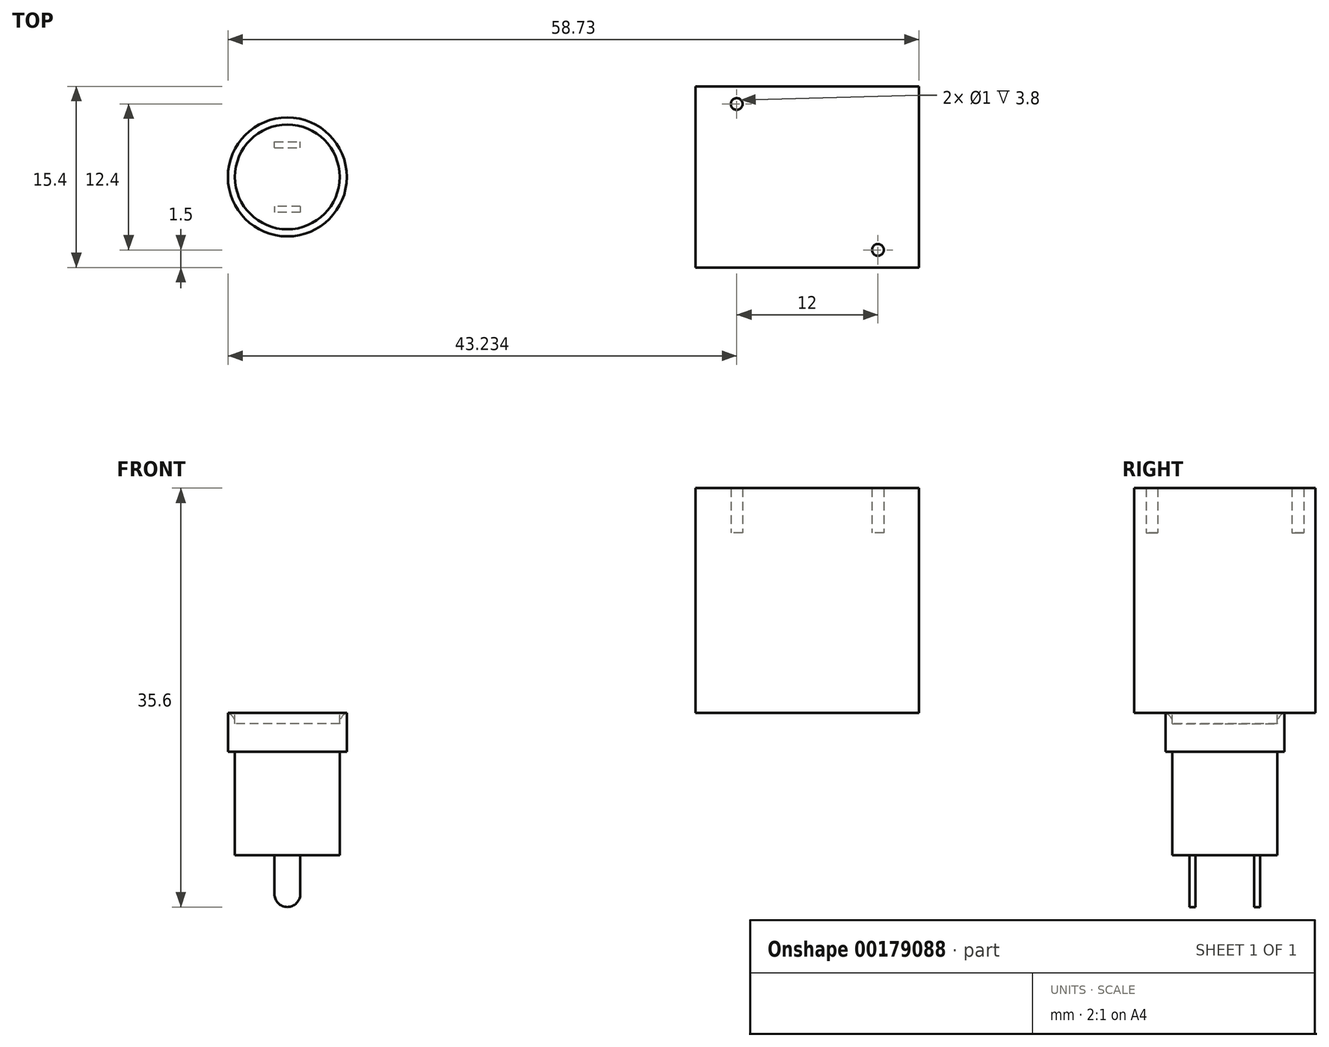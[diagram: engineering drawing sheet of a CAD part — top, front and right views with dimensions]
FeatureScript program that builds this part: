
annotation { "Feature Type Name" : "Feature", "Feature Type Description" : "" }
export const myFeature = defineFeature(function(context is Context, id is Id, definition is map)
    precondition{}
    {
        {
            var Q0;
            Q0=qCreatedBy(makeId("Top.planeOp"),FACE);
            var sketch = newSketch(context, id + "F0", { "sketchPlane" : qUnion([Q0])});
            skCircle(sketch, "E0", {"center": v(0, 0) * mm, "radius": 4.45 * mm});
            skCircle(sketch, "E1", {"center": v(0, 0) * mm, "radius": 5.05 * mm});
            skSolve(sketch);
        }
        {
            var Q0;
            Q0=makeQuery(id+"F0.imprint","IMPRINT",FACE,{"disambiguationData":[TD([[makeQuery(id+"F0.imprint","IMPRINT",EDGE,{"derivedFrom":sQuery(id+"F0.wireOp",EDGE,"E0")}),-1.0]])]});
            extrude(context, id + "F1", {"entities" : qUnion([Q0]), "oppositeDirection" : true, "depth" : 3.3 * mm});
        }
        {
            var Q0;
            Q0=makeQuery(id+"F1.opExtrude","CAP_EDGE",EDGE,{"disambiguationData":[OSD([sQuery(id+"F0.wireOp",EDGE,"E0")])],"isStart":true});
            fillet(context, id + "F2", {"entities" : qUnion([Q0]), "radius" : 1 * mm, "tangentPropagation" : true, "allowEdgeOverflow" : false});
        }
        {
            var Q0;
            Q0=makeQuery(id+"F0.imprint","IMPRINT",FACE,{"disambiguationData":[TD([[makeQuery(id+"F0.imprint","IMPRINT",EDGE,{"derivedFrom":sQuery(id+"F0.wireOp",EDGE,"E0")}),1.0]])]});
            extrude(context, id + "F3", {"entities" : qUnion([Q0]), "operationType" : NewBodyOperationType.ADD, "oppositeDirection" : true, "depth" : 12.1 * mm});
        }
        {
            var Q0;
            Q0=makeQuery(id+"F3.opExtrude","CAP_FACE",FACE,{"disambiguationData":[OSD([sQuery(id+"F0.wireOp",EDGE,"E0")])],"isStart":false});
            var sketch = newSketch(context, id + "F4", { "sketchPlane" : qUnion([Q0])});
            skLineSegment(sketch, "E2", {"start": v(0, 0) * mm, "end": v(0, 2.5) * mm, "construction": true});
            skLineSegment(sketch, "E3", {"start": v(0, 2.5) * mm, "end": v(1.1, 2.5) * mm});
            skLineSegment(sketch, "E4", {"start": v(1.1, 2.5) * mm, "end": v(1.1, 3) * mm});
            skLineSegment(sketch, "E5", {"start": v(1.1, 3) * mm, "end": v(0, 3) * mm});
            skPoint(sketch, "E5.endSnap0", {"position": v(0, 1.25) * mm});
            skLineSegment(sketch, "E6.MirrorCS", {"start": v(-1.1, 3) * mm, "end": v(0, 3) * mm});
            skLineSegment(sketch, "E7.MirrorCS", {"start": v(0, 2.5) * mm, "end": v(-1.1, 2.5) * mm});
            skLineSegment(sketch, "E8.MirrorCS", {"start": v(-1.1, 2.5) * mm, "end": v(-1.1, 3) * mm});
            skLineSegment(sketch, "E9", {"start": v(0, 0) * mm, "end": v(4.45, 0) * mm, "construction": true});
            skLineSegment(sketch, "E10.MirrorCS", {"start": v(-1.1, -3) * mm, "end": v(0, -3) * mm});
            skLineSegment(sketch, "E11.MirrorCS", {"start": v(1.1, -3) * mm, "end": v(0, -3) * mm});
            skLineSegment(sketch, "E12.MirrorCS", {"start": v(1.1, -2.5) * mm, "end": v(1.1, -3) * mm});
            skLineSegment(sketch, "E13.MirrorCS", {"start": v(0, -2.5) * mm, "end": v(1.1, -2.5) * mm});
            skLineSegment(sketch, "E14.MirrorCS", {"start": v(0, -2.5) * mm, "end": v(-1.1, -2.5) * mm});
            skLineSegment(sketch, "E15.MirrorCS", {"start": v(-1.1, -2.5) * mm, "end": v(-1.1, -3) * mm});
            skSolve(sketch);
        }
        {
            var Q0;
            Q0=makeQuery(id+"F4.imprint","IMPRINT",FACE,{"disambiguationData":[TD([[makeQuery(id+"F4.imprint","IMPRINT",EDGE,{"derivedFrom":sQuery(id+"F4.wireOp",EDGE,"E4")}),1.0]])]});
            var Q1;
            Q1=makeQuery(id+"F4.imprint","IMPRINT",FACE,{"disambiguationData":[TD([[makeQuery(id+"F4.imprint","IMPRINT",EDGE,{"derivedFrom":sQuery(id+"F4.wireOp",EDGE,"E10.MirrorCS")}),1.0]])]});
            extrude(context, id + "F5", {"entities" : qUnion([Q0, Q1]), "operationType" : NewBodyOperationType.ADD, "depth" : 4.4 * mm});
        }
        {
            var Q0;
            Q0=makeQuery(id+"F5.opExtrude","CAP_EDGE",EDGE,{"disambiguationData":[OSD([sQuery(id+"F4.wireOp",EDGE,"E8.MirrorCS")])],"isStart":false});
            var Q1;
            Q1=makeQuery(id+"F5.opExtrude","CAP_EDGE",EDGE,{"disambiguationData":[OSD([sQuery(id+"F4.wireOp",EDGE,"E4")])],"isStart":false});
            var Q2;
            Q2=makeQuery(id+"F5.opExtrude","CAP_EDGE",EDGE,{"disambiguationData":[OSD([sQuery(id+"F4.wireOp",EDGE,"E12.MirrorCS")])],"isStart":false});
            var Q3;
            Q3=makeQuery(id+"F5.opExtrude","CAP_EDGE",EDGE,{"disambiguationData":[OSD([sQuery(id+"F4.wireOp",EDGE,"E15.MirrorCS")])],"isStart":false});
            fillet(context, id + "F6", {"entities" : qUnion([Q0, Q1, Q2, Q3]), "radius" : 1.1 * mm, "tangentPropagation" : true, "allowEdgeOverflow" : false});
        }
        {
            var Q0;
            Q0=qCreatedBy(makeId("Top.planeOp"),FACE);
            var sketch = newSketch(context, id + "F7", { "sketchPlane" : qUnion([Q0])});
            skLineSegment(sketch, "E16.bottom", {"start": v(53.68, 7.7) * mm, "end": v(34.68, 7.7) * mm});
            skLineSegment(sketch, "E16.top", {"start": v(53.68, -7.7) * mm, "end": v(34.68, -7.7) * mm});
            skLineSegment(sketch, "E16.left", {"start": v(53.68, 7.7) * mm, "end": v(53.68, -7.7) * mm});
            skLineSegment(sketch, "E16.right", {"start": v(34.68, 7.7) * mm, "end": v(34.68, -7.7) * mm});
            skPoint(sketch, "E16.middle", {"position": v(44.18, 0) * mm});
            skSolve(sketch);
        }
        {
            var Q0;
            Q0=makeQuery(id+"F7.imprint","IMPRINT",FACE,{"disambiguationData":[TD([[makeQuery(id+"F7.imprint","IMPRINT",EDGE,{"derivedFrom":sQuery(id+"F7.wireOp",EDGE,"E16.bottom")}),1.0]])]});
            extrude(context, id + "F8", {"entities" : qUnion([Q0]), "depth" : 15.3 * mm});
        }
        {
            var Q0;
            Q0=makeQuery(id+"F8.opExtrude","CAP_FACE",FACE,{"disambiguationData":[OSD([sQuery(id+"F7.wireOp",EDGE,"E16.bottom"),sQuery(id+"F7.wireOp",EDGE,"E16.top"),sQuery(id+"F7.wireOp",EDGE,"E16.left"),sQuery(id+"F7.wireOp",EDGE,"E16.right")])],"isStart":false});
            var sketch = newSketch(context, id + "F9", { "sketchPlane" : qUnion([Q0])});
            skCircle(sketch, "E17", {"center": v(50.18, 6.2) * mm, "radius": 0.5 * mm});
            skLineSegment(sketch, "E18", {"start": v(50.18, 6.2) * mm, "end": v(50.18, 7.7) * mm, "construction": true});
            skLineSegment(sketch, "E19", {"start": v(50.18, 7.7) * mm, "end": v(53.68, 7.7) * mm, "construction": true});
            skLineSegment(sketch, "E20", {"start": v(53.68, 0) * mm, "end": v(34.68, 0) * mm, "construction": true});
            skLineSegment(sketch, "E21", {"start": v(44.18, 7.7) * mm, "end": v(44.18, -7.7) * mm, "construction": true});
            skCircle(sketch, "E22.MirrorC", {"center": v(38.18, 6.2) * mm, "radius": 0.5 * mm});
            skLineSegment(sketch, "E23.MirrorCS", {"start": v(34.68, 0) * mm, "end": v(53.68, 0) * mm, "construction": true});
            skCircle(sketch, "E24.MirrorC", {"center": v(38.18, -6.2) * mm, "radius": 0.5 * mm});
            skCircle(sketch, "E25.MirrorC", {"center": v(50.18, -6.2) * mm, "radius": 0.5 * mm});
            skCircle(sketch, "E26", {"center": v(35.68, 0) * mm, "radius": 0.5 * mm});
            skLineSegment(sketch, "E27", {"start": v(35.68, 0) * mm, "end": v(34.68, 0) * mm, "construction": true});
            skSolve(sketch);
        }
        {
            var Q0;
            Q0=makeQuery(id+"F9.imprint","IMPRINT",FACE,{"disambiguationData":[TD([[makeQuery(id+"F9.imprint","IMPRINT",EDGE,{"derivedFrom":sQuery(id+"F9.wireOp",EDGE,"E17")}),1.0]])]});
            var Q1;
            Q1=makeQuery(id+"F9.imprint","IMPRINT",FACE,{"disambiguationData":[TD([[makeQuery(id+"F9.imprint","IMPRINT",EDGE,{"derivedFrom":sQuery(id+"F9.wireOp",EDGE,"E24.MirrorC")}),1.0]])]});
            var Q2;
            Q2=makeQuery(id+"F9.imprint","IMPRINT",FACE,{"disambiguationData":[TD([[makeQuery(id+"F9.imprint","IMPRINT",EDGE,{"derivedFrom":sQuery(id+"F9.wireOp",EDGE,"E25.MirrorC")}),-1.0]])]});
            var Q3;
            Q3=makeQuery(id+"F9.imprint","IMPRINT",FACE,{"disambiguationData":[TD([[makeQuery(id+"F9.imprint","IMPRINT",EDGE,{"derivedFrom":sQuery(id+"F9.wireOp",EDGE,"E26")}),1.0]])]});
            var Q4;
            Q4=makeQuery(id+"F9.imprint","IMPRINT",FACE,{"disambiguationData":[TD([[makeQuery(id+"F9.imprint","IMPRINT",EDGE,{"derivedFrom":sQuery(id+"F9.wireOp",EDGE,"E22.MirrorC")}),-1.0]])]});
            extrude(context, id + "F10", {"entities" : qUnion([Q0, Q1, Q2, Q3, Q4]), "operationType" : NewBodyOperationType.ADD, "depth" : 3.8 * mm});
        }
    });
